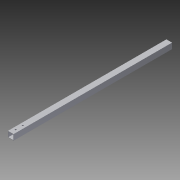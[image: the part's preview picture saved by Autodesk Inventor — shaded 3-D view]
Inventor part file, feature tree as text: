
AUTODESK INVENTOR PART (.ipt)
format: ipt  version: 2013 (Build 170138000, 138)  size: 90,112 bytes
history: native  units: in
note: dims shown in document units (in); Inventor stores cm internally (conversion verified against a paired STEP export)
features: reference x4, extrude x3, sketch x3
ambient origin geometry x8: Origin, YZ Plane, XZ Plane, XY Plane, X Axis, Y Axis, Z Axis, Center Point
bodies: Solid1 (feature_tree)
feature tree (10):
  extrude  "Extrusion1"  Depth=1.0in
  extrude  "Extrusion3"  Depth=23.5in TaperAngle=0.0deg
  extrude  "Extrusion4"  Depth=1.0in TaperAngle=0.0deg
  sketch  "Sketch1"  dims[d0=1.0in d2=1.0in]
  sketch  "Sketch3"  dims[d3=0.0625in d4=23.5in d5=0.0in]
  reference  "Reference3"
  reference  "Reference4"
  sketch  "Sketch4"  dims[d8=1.0in d9=0.0in d10=1.0in d11=0.0in]
  reference  "Reference5"
  reference  "Reference6"
